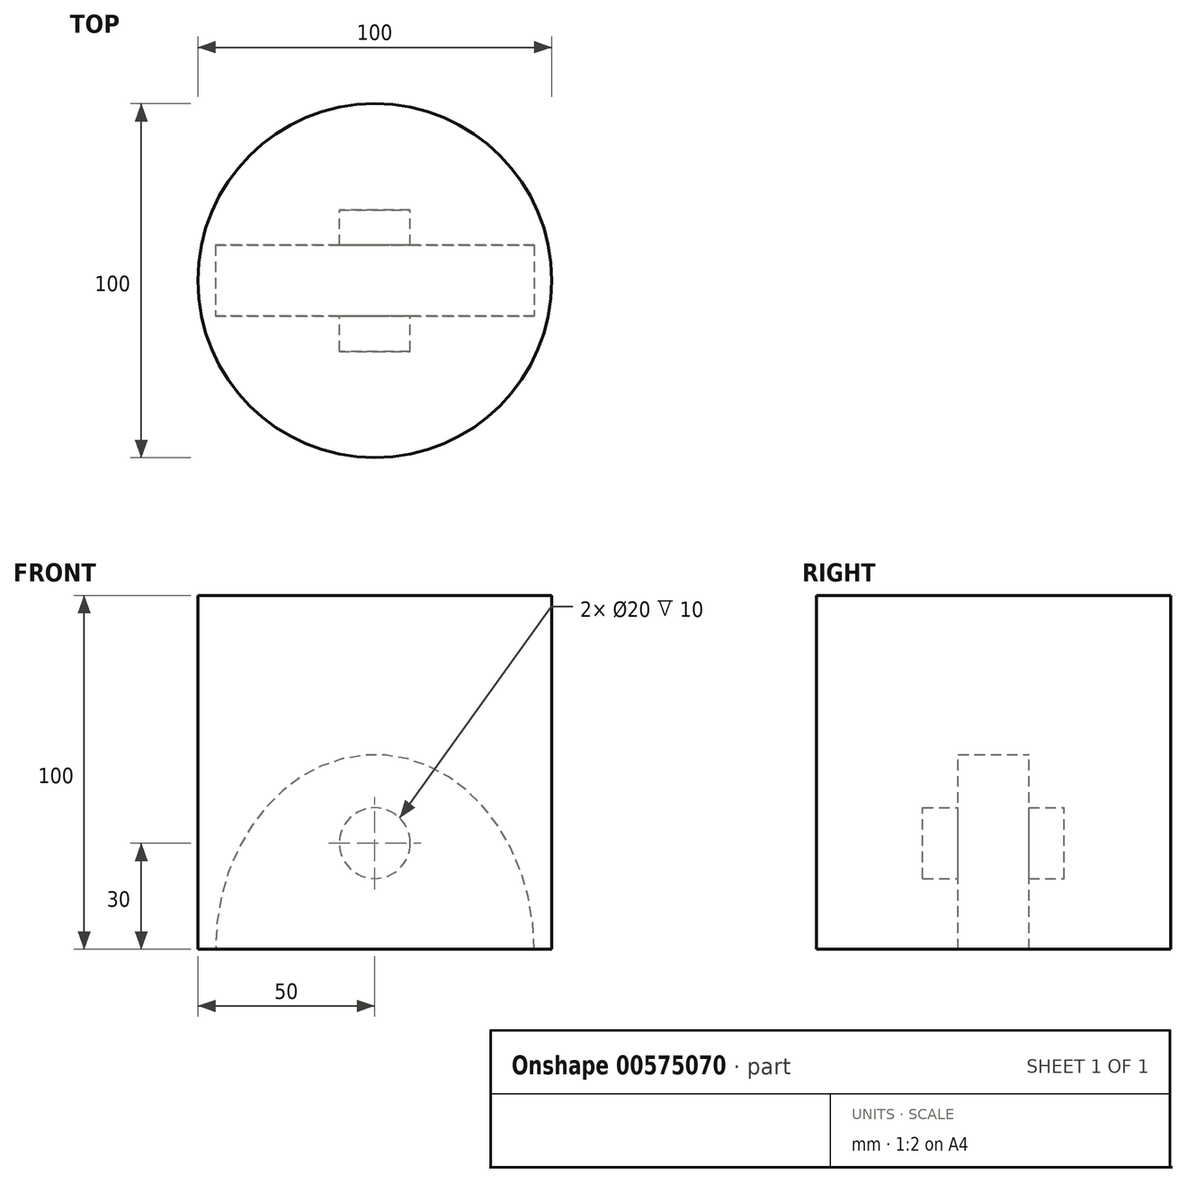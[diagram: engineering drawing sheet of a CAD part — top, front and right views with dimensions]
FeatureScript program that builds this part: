
annotation { "Feature Type Name" : "Feature", "Feature Type Description" : "" }
export const myFeature = defineFeature(function(context is Context, id is Id, definition is map)
    precondition{}
    {
        {
            var Q0;
            Q0=qCreatedBy(makeId("Top.planeOp"),FACE);
            var sketch = newSketch(context, id + "F0", { "sketchPlane" : qUnion([Q0])});
            skCircle(sketch, "E0", {"center": v(0, 0) * mm, "radius": 50 * mm});
            skSolve(sketch);
        }
        {
            var Q0;
            Q0=makeQuery(id+"F0.imprint","IMPRINT",FACE,{"disambiguationData":[TD([[makeQuery(id+"F0.imprint","IMPRINT",EDGE,{"derivedFrom":sQuery(id+"F0.wireOp",EDGE,"E0")}),1.0]])]});
            extrude(context, id + "F1", {"entities" : qUnion([Q0]), "depth" : 100 * mm, "offsetDistance" : 25 * mm});
        }
        {
            var Q0;
            Q0=qCreatedBy(makeId("Front.planeOp"),FACE);
            var sketch = newSketch(context, id + "F2", { "sketchPlane" : qUnion([Q0])});
            skEllipse(sketch, "E1", {"center": v(0, 0) * mm, "majorRadius": 55 * mm, "minorRadius": 45 * mm, "majorAxis": v(0, 1)});
            skSolve(sketch);
        }
        {
            var Q0;
            Q0=makeQuery(id+"F2.imprint","IMPRINT",FACE,{"disambiguationData":[TD([[makeQuery(id+"F2.imprint","IMPRINT",EDGE,{"derivedFrom":sQuery(id+"F2.wireOp",EDGE,"E1")}),1.0]])]});
            var Q1;
            Q1=sQuery(id+"F2.wireOp",EDGE,"E1");
            extrude(context, id + "F3", {"entities" : qUnion([Q0]), "operationType" : NewBodyOperationType.REMOVE, "surfaceEntities" : qUnion([Q1]), "oppositeDirection" : true, "depth" : 20 * mm, "offsetDistance" : 25 * mm, "symmetric" : true});
        }
        {
            var Q0;
            Q0=qCreatedBy(makeId("Front.planeOp"),FACE);
            var sketch = newSketch(context, id + "F4", { "sketchPlane" : qUnion([Q0])});
            skCircle(sketch, "E2", {"center": v(0, 30) * mm, "radius": 10 * mm});
            skSolve(sketch);
        }
        {
            var Q0;
            Q0=makeQuery(id+"F4.imprint","IMPRINT",FACE,{"disambiguationData":[TD([[makeQuery(id+"F4.imprint","IMPRINT",EDGE,{"derivedFrom":sQuery(id+"F4.wireOp",EDGE,"E2")}),1.0]])]});
            extrude(context, id + "F5", {"entities" : qUnion([Q0]), "operationType" : NewBodyOperationType.REMOVE, "depth" : 40 * mm, "offsetDistance" : 25 * mm, "symmetric" : true});
        }
    });
